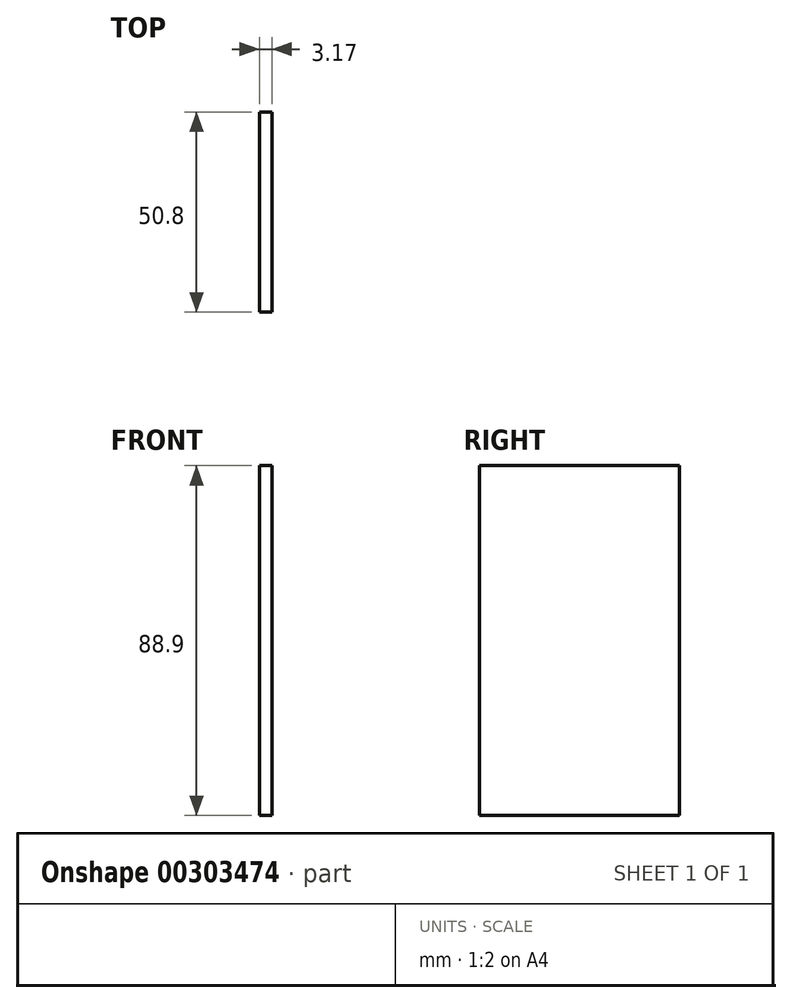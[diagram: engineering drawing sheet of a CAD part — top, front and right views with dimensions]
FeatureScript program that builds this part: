
annotation { "Feature Type Name" : "Feature", "Feature Type Description" : "" }
export const myFeature = defineFeature(function(context is Context, id is Id, definition is map)
    precondition{}
    {
        {
            var Q0;
            Q0=qCreatedBy(makeId("Right.planeOp"),FACE);
            var sketch = newSketch(context, id + "F0", { "sketchPlane" : qUnion([Q0])});
            skLineSegment(sketch, "E0.bottom", {"start": v(-25.4, 44.45) * mm, "end": v(25.4, 44.45) * mm});
            skLineSegment(sketch, "E0.top", {"start": v(-25.4, -44.45) * mm, "end": v(25.4, -44.45) * mm});
            skLineSegment(sketch, "E0.left", {"start": v(-25.4, 44.45) * mm, "end": v(-25.4, -44.45) * mm});
            skLineSegment(sketch, "E0.right", {"start": v(25.4, 44.45) * mm, "end": v(25.4, -44.45) * mm});
            skPoint(sketch, "E0.middle", {"position": v(0, 0) * mm});
            skSolve(sketch);
        }
        {
            var Q0;
            Q0 = qSketchRegion(id + "F0", true);
            extrude(context, id + "F1", {"entities" : qUnion([Q0]), "depth" : 3.17 * mm});
        }
    });
